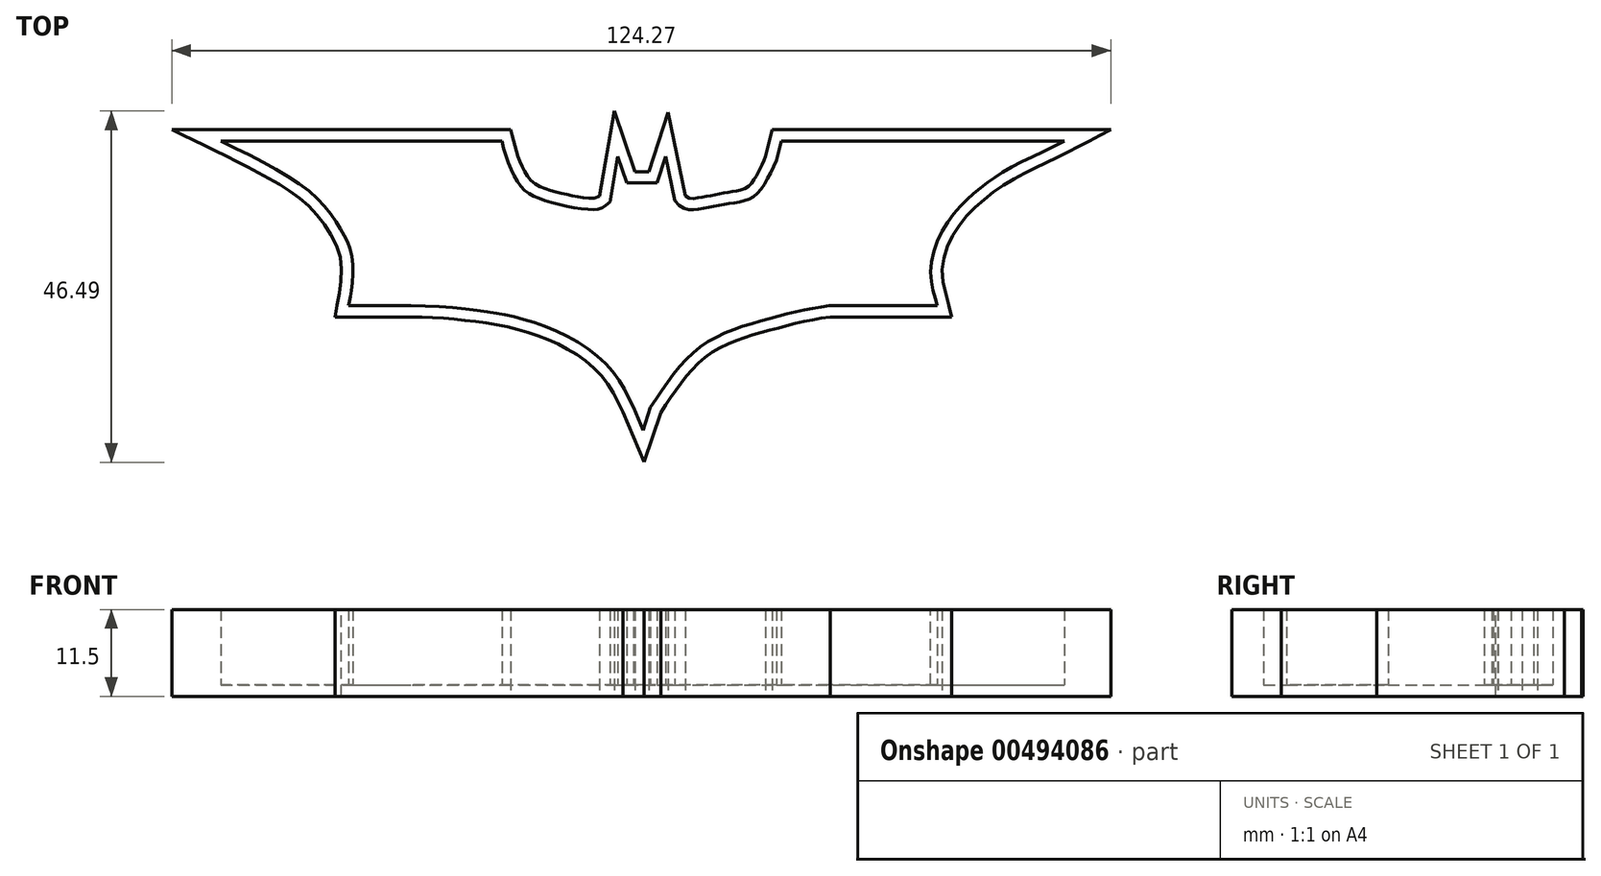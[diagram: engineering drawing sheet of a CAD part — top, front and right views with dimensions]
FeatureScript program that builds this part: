
annotation { "Feature Type Name" : "Feature", "Feature Type Description" : "" }
export const myFeature = defineFeature(function(context is Context, id is Id, definition is map)
    precondition{}
    {
        {
            var Q0;
            Q0=qCreatedBy(makeId("Top.planeOp"),FACE);
            var sketch = newSketch(context, id + "F0", { "sketchPlane" : qUnion([Q0])});
            skLineSegment(sketch, "E0", {"start": v(-55.83, 45.23) * mm, "end": v(-18.67, 45.23) * mm});
            skLineSegment(sketch, "E1", {"start": v(18.3, 45.23) * mm, "end": v(55.77, 45.23) * mm});
            skLineSegment(sketch, "E2", {"start": v(-4.36, 37.17) * mm, "end": v(-3.32, 43.18) * mm});
            skLineSegment(sketch, "E3", {"start": v(-3.32, 43.18) * mm, "end": v(-2.13, 39.69) * mm});
            skLineSegment(sketch, "E4", {"start": v(-2.13, 39.69) * mm, "end": v(1.9, 39.69) * mm});
            skLineSegment(sketch, "E5", {"start": v(1.9, 39.69) * mm, "end": v(3, 43.18) * mm});
            skLineSegment(sketch, "E6", {"start": v(3, 43.18) * mm, "end": v(4.24, 37.34) * mm});
            skLineSegment(sketch, "E7", {"start": v(17.66, 42.68) * mm, "end": v(18.3, 45.23) * mm});
            skLineSegment(sketch, "E8", {"start": v(38.95, 23.43) * mm, "end": v(24.69, 23.43) * mm});
            skLineSegment(sketch, "E9", {"start": v(-38.98, 23.43) * mm, "end": v(-30.7, 23.43) * mm});
            skLineSegment(sketch, "E10", {"start": v(0, 6.96) * mm, "end": v(-1.27, 9.96) * mm});
            skLineSegment(sketch, "E11", {"start": v(0, 6.96) * mm, "end": v(1, 9.96) * mm});
            skFitSpline(sketch, "E12", {"points": [v(24.69, 23.43) * mm, v(16.51, 21.67) * mm, v(7.66, 18.03) * mm, v(1, 9.96) * mm], "startDerivative": vector(-25.67, -2.85) * mm, "endDerivative": vector(-16.9, -25.79) * mm});
            skFitSpline(sketch, "E13", {"points": [v(-1.27, 9.96) * mm, v(-4.22, 15) * mm, v(-10.16, 19.49) * mm, v(-16.82, 21.91) * mm, v(-21.4, 22.74) * mm, v(-30.7, 23.43) * mm], "startDerivative": vector(-13.12, 27.99) * mm, "endDerivative": vector(-43.07, -0.4) * mm});
            skFitSpline(sketch, "E14", {"points": [v(-38.98, 23.43) * mm, v(-38.66, 25.02) * mm, v(-38.49, 29.84) * mm, v(-39.86, 33.34) * mm, v(-43.74, 38.23) * mm, v(-55.83, 45.23) * mm], "startDerivative": vector(2.49, 14.97) * mm, "endDerivative": vector(-43.96, 21.34) * mm});
            skFitSpline(sketch, "E15", {"points": [v(38.95, 23.43) * mm, v(38.07, 27.9) * mm, v(40.23, 34.39) * mm, v(44.13, 38.57) * mm, v(48.28, 41.5) * mm, v(55.77, 45.23) * mm], "startDerivative": vector(-5.3, 21.37) * mm, "endDerivative": vector(29.88, 15.5) * mm});
            skFitSpline(sketch, "E16", {"points": [v(-18.67, 45.23) * mm, v(-16.28, 39.41) * mm, v(-13.04, 37.4) * mm, v(-6.73, 36.16) * mm, v(-4.36, 37.17) * mm], "startDerivative": vector(5.03, -21.33) * mm, "endDerivative": vector(13.14, 12.58) * mm});
            skFitSpline(sketch, "E17", {"points": [v(4.24, 37.34) * mm, v(7.58, 36.24) * mm, v(11.36, 36.95) * mm, v(14.82, 38.01) * mm, v(17.66, 42.68) * mm], "startDerivative": vector(12.42, -17.96) * mm, "endDerivative": vector(8.87, 19.1) * mm});
            skSolve(sketch);
        }
        {
            var Q0;
            Q0=makeQuery(id+"F0.imprint","IMPRINT",FACE,{"disambiguationData":[TD([[makeQuery(id+"F0.imprint","IMPRINT",EDGE,{"derivedFrom":sQuery(id+"F0.wireOp",EDGE,"E0")}),-1.0]])]});
            extrude(context, id + "F1", {"entities" : qUnion([Q0]), "depth" : 10 * mm});
        }
        {
            var Q0;
            Q0=makeQuery(id+"F1.opExtrude","CAP_FACE",FACE,{"disambiguationData":[OSD([sQuery(id+"F0.wireOp",EDGE,"E0"),sQuery(id+"F0.wireOp",EDGE,"E1"),sQuery(id+"F0.wireOp",EDGE,"E2"),sQuery(id+"F0.wireOp",EDGE,"E3"),sQuery(id+"F0.wireOp",EDGE,"E4"),sQuery(id+"F0.wireOp",EDGE,"E5"),sQuery(id+"F0.wireOp",EDGE,"E6"),sQuery(id+"F0.wireOp",EDGE,"E7"),sQuery(id+"F0.wireOp",EDGE,"E8"),sQuery(id+"F0.wireOp",EDGE,"E9"),sQuery(id+"F0.wireOp",EDGE,"E10"),sQuery(id+"F0.wireOp",EDGE,"E11"),sQuery(id+"F0.wireOp",EDGE,"E12"),sQuery(id+"F0.wireOp",EDGE,"E13"),sQuery(id+"F0.wireOp",EDGE,"E14"),sQuery(id+"F0.wireOp",EDGE,"E15"),sQuery(id+"F0.wireOp",EDGE,"E16"),sQuery(id+"F0.wireOp",EDGE,"E17")])],"isStart":false});
            shell(context, id + "F2", {"entities" : qUnion([Q0]), "thickness" : 1.5 * mm, "oppositeDirection" : true});
        }
        {
            var Q0;
            Q0=makeQuery(id+"F2.opShell","OFFSET_FACE",FACE,{"disambiguationData":[OSD([sQuery(id+"F0.wireOp",EDGE,"E0"),sQuery(id+"F0.wireOp",EDGE,"E1"),sQuery(id+"F0.wireOp",EDGE,"E2"),sQuery(id+"F0.wireOp",EDGE,"E3"),sQuery(id+"F0.wireOp",EDGE,"E4"),sQuery(id+"F0.wireOp",EDGE,"E5"),sQuery(id+"F0.wireOp",EDGE,"E6"),sQuery(id+"F0.wireOp",EDGE,"E7"),sQuery(id+"F0.wireOp",EDGE,"E8"),sQuery(id+"F0.wireOp",EDGE,"E9"),sQuery(id+"F0.wireOp",EDGE,"E10"),sQuery(id+"F0.wireOp",EDGE,"E11"),sQuery(id+"F0.wireOp",EDGE,"E12"),sQuery(id+"F0.wireOp",EDGE,"E13"),sQuery(id+"F0.wireOp",EDGE,"E14"),sQuery(id+"F0.wireOp",EDGE,"E15"),sQuery(id+"F0.wireOp",EDGE,"E16"),sQuery(id+"F0.wireOp",EDGE,"E17")])]});
            var sketch = newSketch(context, id + "F3", { "sketchPlane" : qUnion([Q0])});
            skCircle(sketch, "E18", {"center": v(0, 26.39) * mm, "radius": 8.75 * mm});
            skSolve(sketch);
        }
        {
            var Q0;
            Q0=sQuery(id+"F3.wireOp",EDGE,"E18");
            extrude(context, id + "F4", {"bodyType" : ToolBodyType.SURFACE, "operationType" : NewBodyOperationType.REMOVE, "surfaceEntities" : qUnion([Q0]), "oppositeDirection" : true, "depth" : 25 * mm});
        }
    });
